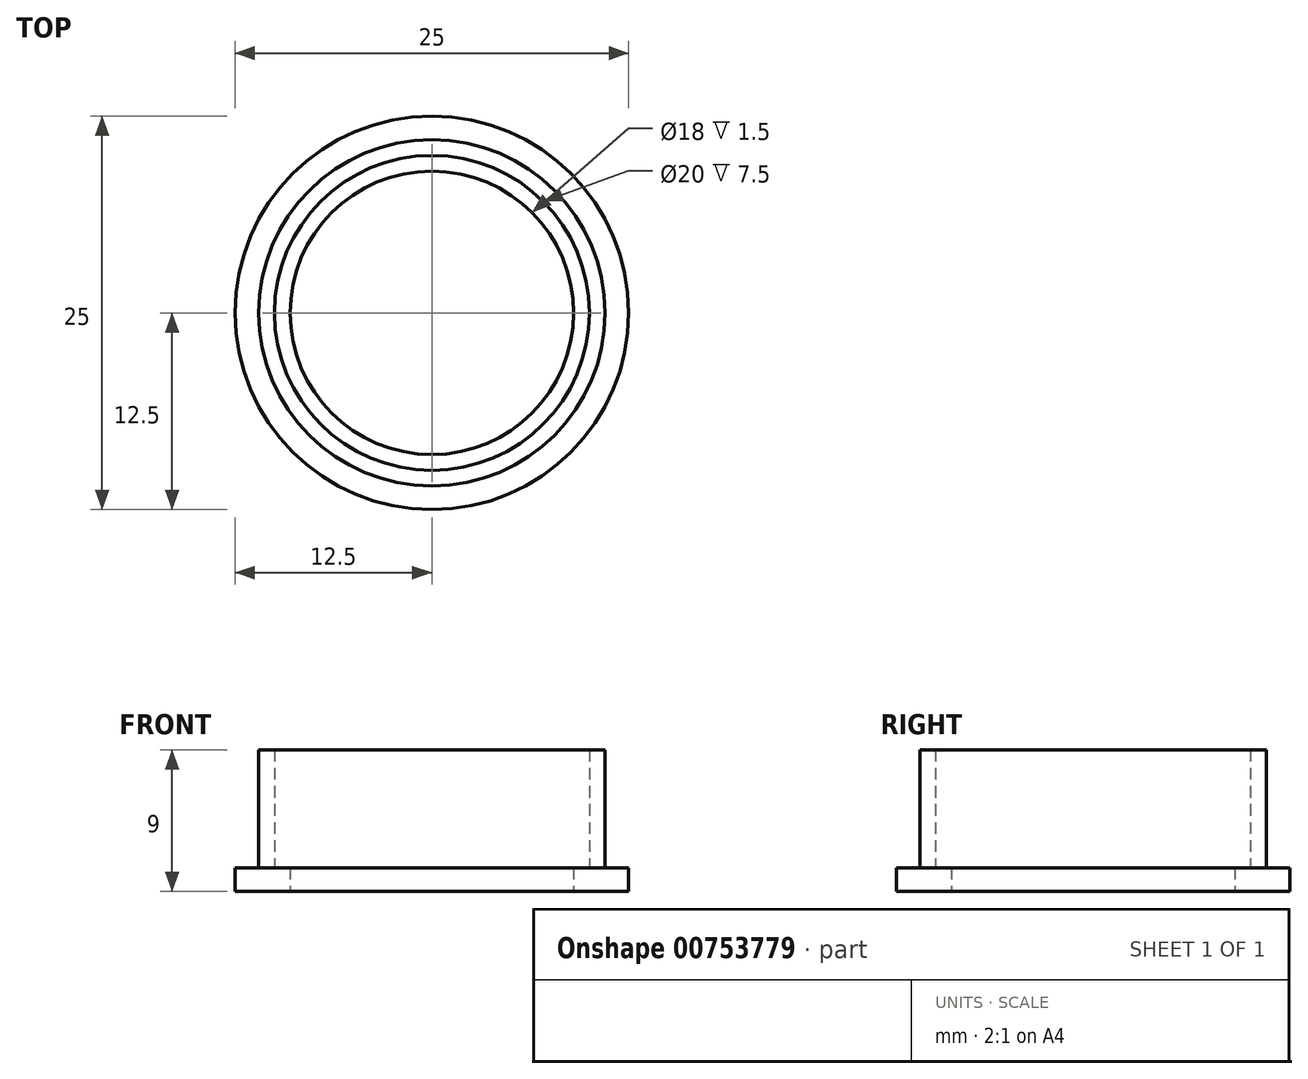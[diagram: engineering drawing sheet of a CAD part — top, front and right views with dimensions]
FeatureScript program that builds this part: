
annotation { "Feature Type Name" : "Feature", "Feature Type Description" : "" }
export const myFeature = defineFeature(function(context is Context, id is Id, definition is map)
    precondition{}
    {
        {
            var Q0;
            Q0=qCreatedBy(makeId("Front.planeOp"),FACE);
            var sketch = newSketch(context, id + "F0", { "sketchPlane" : qUnion([Q0])});
            skLineSegment(sketch, "E0", {"start": v(0, 0) * mm, "end": v(-9, 0) * mm});
            skLineSegment(sketch, "E1", {"start": v(-9, 0) * mm, "end": v(-9, 1.5) * mm});
            skLineSegment(sketch, "E2", {"start": v(-9, 1.5) * mm, "end": v(-10, 1.5) * mm});
            skLineSegment(sketch, "E3", {"start": v(-10, 1.5) * mm, "end": v(-10, 9) * mm});
            skLineSegment(sketch, "E4", {"start": v(-10, 9) * mm, "end": v(-11, 9) * mm});
            skLineSegment(sketch, "E5", {"start": v(-11, 9) * mm, "end": v(-11, 1.5) * mm});
            skLineSegment(sketch, "E6", {"start": v(0, 15.6) * mm, "end": v(-12, 15.6) * mm});
            skLineSegment(sketch, "E7", {"start": v(0, 0) * mm, "end": v(0, 8.26) * mm});
            skLineSegment(sketch, "E8", {"start": v(-11, 1.5) * mm, "end": v(-12.5, 1.5) * mm});
            skLineSegment(sketch, "E9", {"start": v(-9, 0) * mm, "end": v(-12.5, 0) * mm});
            skLineSegment(sketch, "E10", {"start": v(-12.5, 0) * mm, "end": v(-12.5, 1.5) * mm});
            skSolve(sketch);
        }
        {
            var Q0;
            Q0=makeQuery(id+"F0.imprint","IMPRINT",FACE,{"disambiguationData":[TD([[makeQuery(id+"F0.imprint","IMPRINT",EDGE,{"derivedFrom":sQuery(id+"F0.wireOp",EDGE,"E1")}),1.0]])]});
            var Q1;
            Q1=sQuery(id+"F0.wireOp",EDGE,"E7");
            revolve(context, id + "F1", {"surfaceOperationType" : NewSurfaceOperationType.NEW, "entities" : qUnion([Q0]), "axis" : qUnion([Q1]), "revolveType" : RevolveType.FULL});
        }
    });
